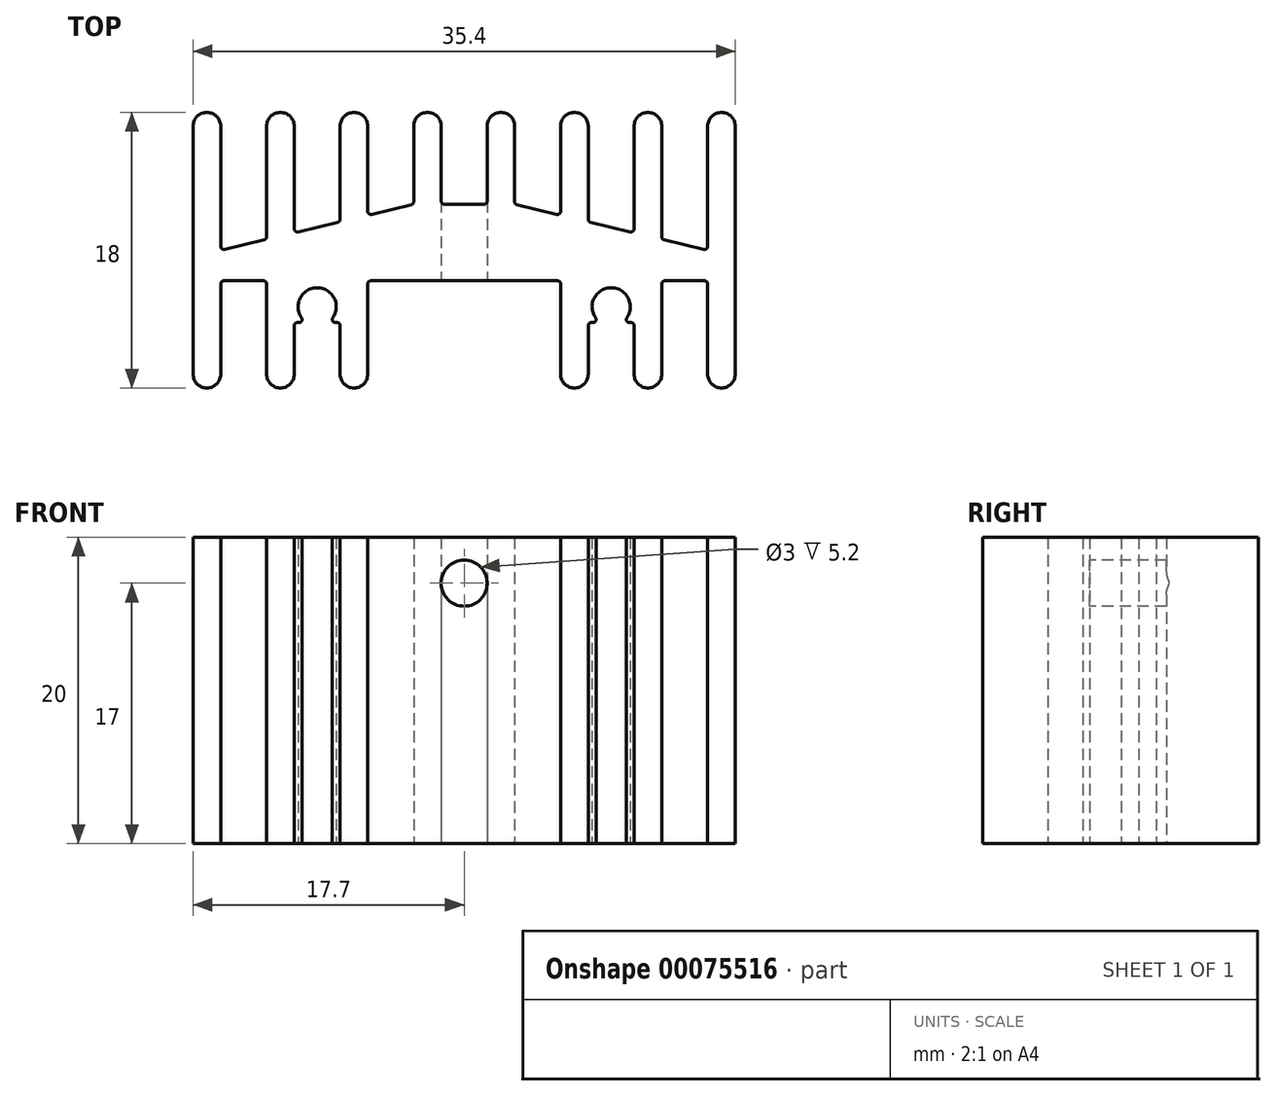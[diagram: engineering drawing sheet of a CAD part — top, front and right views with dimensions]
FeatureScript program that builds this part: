
annotation { "Feature Type Name" : "Feature", "Feature Type Description" : "" }
export const myFeature = defineFeature(function(context is Context, id is Id, definition is map)
    precondition{}
    {
        {
            var Q0;
            Q0=qCreatedBy(makeId("Top.planeOp"),FACE);
            var sketch = newSketch(context, id + "F0", { "sketchPlane" : qUnion([Q0])});
            skLineSegment(sketch, "E0", {"start": v(-17.7, 0) * mm, "end": v(-17.7, 10.1) * mm});
            skLineSegment(sketch, "E1", {"start": v(-17.7, 0) * mm, "end": v(-17.7, -6.1) * mm});
            skLineSegment(sketch, "E2.0", {"start": v(-15.9, -6.1) * mm, "end": v(-15.9, -2.93) * mm});
            skLineSegment(sketch, "E3.0", {"start": v(-12.9, -6.1) * mm, "end": v(-12.9, -2.93) * mm});
            skLineSegment(sketch, "E4.0", {"start": v(-11.1, -6.1) * mm, "end": v(-11.1, -2.93) * mm});
            skLineSegment(sketch, "E5.0", {"start": v(-8.1, -6.1) * mm, "end": v(-8.1, -2.93) * mm});
            skLineSegment(sketch, "E6.0", {"start": v(-6.3, -6.1) * mm, "end": v(-6.3, -0.2) * mm});
            skLineSegment(sketch, "E7.0", {"start": v(-3.3, 5.16) * mm, "end": v(-3.3, 10.1) * mm});
            skLineSegment(sketch, "E8.0", {"start": v(-1.5, 5.2) * mm, "end": v(-1.5, 10.1) * mm});
            skLineSegment(sketch, "E9", {"start": v(-16.8, -7) * mm, "end": v(-16.8, -7) * mm});
            skLineSegment(sketch, "E10", {"start": v(-16.8, 11) * mm, "end": v(-16.8, 11) * mm});
            skLineSegment(sketch, "E11.trimOffspring", {"start": v(-12, 11) * mm, "end": v(-12, 11) * mm});
            skLineSegment(sketch, "E12.trimOffspring", {"start": v(-7.2, 11) * mm, "end": v(-7.2, 11) * mm});
            skLineSegment(sketch, "E13.trimOffspring", {"start": v(-2.4, 11) * mm, "end": v(-2.4, 11) * mm});
            skLineSegment(sketch, "E14.trimOffspring", {"start": v(-7.2, -7) * mm, "end": v(-7.2, -7) * mm});
            skLineSegment(sketch, "E15.trimOffspring", {"start": v(-12, -7) * mm, "end": v(-12, -7) * mm});
            skPoint(sketch, "E16.orphan", {"position": v(0, -7) * mm});
            skLineSegment(sketch, "E17", {"start": v(-15.65, 2.06) * mm, "end": v(-13.05, 2.68) * mm});
            skLineSegment(sketch, "E18.trimOffspring", {"start": v(-11.1, 3.4) * mm, "end": v(-11.1, 10.1) * mm});
            skLineSegment(sketch, "E19.trimOffspring", {"start": v(-12.9, 2.87) * mm, "end": v(-12.9, 10.1) * mm});
            skLineSegment(sketch, "E20.trimOffspring", {"start": v(-8.1, 4.02) * mm, "end": v(-8.1, 10.1) * mm});
            skLineSegment(sketch, "E21.trimOffspring", {"start": v(-6.3, 4.54) * mm, "end": v(-6.3, 10.1) * mm});
            skLineSegment(sketch, "E22.trimOffspring", {"start": v(-6.05, 4.34) * mm, "end": v(-3.45, 4.96) * mm});
            skLineSegment(sketch, "E23.trimOffspring", {"start": v(-10.85, 3.2) * mm, "end": v(-8.25, 3.82) * mm});
            skLineSegment(sketch, "E24.trimOffspring", {"start": v(-15.9, 2.25) * mm, "end": v(-15.9, 10.1) * mm});
            skPoint(sketch, "E25.centerSnap0", {"position": v(-14.4, 0) * mm});
            skPoint(sketch, "E26.visualSharp", {"position": v(-1.5, 11) * mm});
            skArc(sketch, "E26.filletArc", {"start": v(-1.5, 10.1) * mm, "mid": v(-1.76, 10.74) * mm, "end": v(-2.4, 11) * mm});
            skPoint(sketch, "E27.visualSharp", {"position": v(-3.3, 11) * mm});
            skArc(sketch, "E27.filletArc", {"start": v(-2.4, 11) * mm, "mid": v(-3.04, 10.74) * mm, "end": v(-3.3, 10.1) * mm});
            skPoint(sketch, "E28.visualSharp", {"position": v(-6.3, 11) * mm});
            skArc(sketch, "E28.filletArc", {"start": v(-6.3, 10.1) * mm, "mid": v(-6.56, 10.74) * mm, "end": v(-7.2, 11) * mm});
            skPoint(sketch, "E29.visualSharp", {"position": v(-8.1, 11) * mm});
            skArc(sketch, "E29.filletArc", {"start": v(-7.2, 11) * mm, "mid": v(-7.84, 10.74) * mm, "end": v(-8.1, 10.1) * mm});
            skPoint(sketch, "E30.visualSharp", {"position": v(-11.1, 11) * mm});
            skArc(sketch, "E30.filletArc", {"start": v(-11.1, 10.1) * mm, "mid": v(-11.36, 10.74) * mm, "end": v(-12, 11) * mm});
            skPoint(sketch, "E31.visualSharp", {"position": v(-12.9, 11) * mm});
            skArc(sketch, "E31.filletArc", {"start": v(-12, 11) * mm, "mid": v(-12.64, 10.74) * mm, "end": v(-12.9, 10.1) * mm});
            skPoint(sketch, "E32.visualSharp", {"position": v(-15.9, 11) * mm});
            skArc(sketch, "E32.filletArc", {"start": v(-15.9, 10.1) * mm, "mid": v(-16.16, 10.74) * mm, "end": v(-16.8, 11) * mm});
            skPoint(sketch, "E33.visualSharp", {"position": v(-17.7, 11) * mm});
            skArc(sketch, "E33.filletArc", {"start": v(-16.8, 11) * mm, "mid": v(-17.44, 10.74) * mm, "end": v(-17.7, 10.1) * mm});
            skPoint(sketch, "E34.visualSharp", {"position": v(-17.7, -7) * mm});
            skArc(sketch, "E34.filletArc", {"start": v(-17.7, -6.1) * mm, "mid": v(-17.44, -6.74) * mm, "end": v(-16.8, -7) * mm});
            skPoint(sketch, "E35.visualSharp", {"position": v(-15.9, -7) * mm});
            skArc(sketch, "E35.filletArc", {"start": v(-16.8, -7) * mm, "mid": v(-16.16, -6.74) * mm, "end": v(-15.9, -6.1) * mm});
            skPoint(sketch, "E36.visualSharp", {"position": v(-12.9, -7) * mm});
            skArc(sketch, "E36.filletArc", {"start": v(-12.9, -6.1) * mm, "mid": v(-12.64, -6.74) * mm, "end": v(-12, -7) * mm});
            skPoint(sketch, "E37.visualSharp", {"position": v(-11.1, -7) * mm});
            skArc(sketch, "E37.filletArc", {"start": v(-12, -7) * mm, "mid": v(-11.36, -6.74) * mm, "end": v(-11.1, -6.1) * mm});
            skPoint(sketch, "E38.visualSharp", {"position": v(-8.1, -7) * mm});
            skArc(sketch, "E38.filletArc", {"start": v(-8.1, -6.1) * mm, "mid": v(-7.84, -6.74) * mm, "end": v(-7.2, -7) * mm});
            skPoint(sketch, "E39.visualSharp", {"position": v(-6.3, -7) * mm});
            skArc(sketch, "E39.filletArc", {"start": v(-7.2, -7) * mm, "mid": v(-6.56, -6.74) * mm, "end": v(-6.3, -6.1) * mm});
            skPoint(sketch, "E40.visualSharp", {"position": v(-12.9, 2.71) * mm});
            skArc(sketch, "E40.filletArc", {"start": v(-13.05, 2.68) * mm, "mid": v(-12.94, 2.75) * mm, "end": v(-12.9, 2.87) * mm});
            skPoint(sketch, "E41.visualSharp", {"position": v(-15.9, 2) * mm});
            skArc(sketch, "E41.filletArc", {"start": v(-15.9, 2.25) * mm, "mid": v(-15.82, 2.1) * mm, "end": v(-15.65, 2.06) * mm});
            skPoint(sketch, "E42.visualSharp", {"position": v(-11.1, 3.14) * mm});
            skArc(sketch, "E42.filletArc", {"start": v(-11.1, 3.4) * mm, "mid": v(-11.02, 3.24) * mm, "end": v(-10.85, 3.2) * mm});
            skPoint(sketch, "E43.visualSharp", {"position": v(-8.1, 3.86) * mm});
            skArc(sketch, "E43.filletArc", {"start": v(-8.25, 3.82) * mm, "mid": v(-8.14, 3.9) * mm, "end": v(-8.1, 4.02) * mm});
            skPoint(sketch, "E44.visualSharp", {"position": v(-6.3, 4.29) * mm});
            skArc(sketch, "E44.filletArc", {"start": v(-6.3, 4.54) * mm, "mid": v(-6.22, 4.38) * mm, "end": v(-6.05, 4.34) * mm});
            skPoint(sketch, "E45.visualSharp", {"position": v(-3.3, 5) * mm});
            skArc(sketch, "E45.filletArc", {"start": v(-3.45, 4.96) * mm, "mid": v(-3.34, 5.03) * mm, "end": v(-3.3, 5.16) * mm});
            skPoint(sketch, "E46.visualSharp", {"position": v(-1.5, 5) * mm});
            skArc(sketch, "E46.filletArc", {"start": v(-1.5, 5.2) * mm, "mid": v(-1.44, 5.06) * mm, "end": v(-1.3, 5) * mm});
            skPoint(sketch, "E47.visualSharp", {"position": v(-6.3, 0) * mm});
            skArc(sketch, "E47.filletArc", {"start": v(-6.1, 0) * mm, "mid": v(-6.24, -0.06) * mm, "end": v(-6.3, -0.2) * mm});
            skPoint(sketch, "E48.visualSharp", {"position": v(-8.1, 0) * mm});
            skPoint(sketch, "E49.visualSharp", {"position": v(-11.1, 0) * mm});
            skPoint(sketch, "E50.orphan", {"position": v(-15.9, 0) * mm});
            skPoint(sketch, "E51.orphan", {"position": v(-12.9, 0) * mm});
            skPoint(sketch, "E52.visualSharp", {"position": v(-15.9, -2.73) * mm});
            skPoint(sketch, "E53.visualSharp", {"position": v(-12.9, -2.73) * mm});
            skArc(sketch, "E54.MirrorCS", {"start": v(1.5, 5.2) * mm, "mid": v(1.44, 5.06) * mm, "end": v(1.3, 5) * mm});
            skArc(sketch, "E55.MirrorCS", {"start": v(13.05, 2.68) * mm, "mid": v(12.94, 2.75) * mm, "end": v(12.9, 2.87) * mm});
            skArc(sketch, "E56.MirrorCS", {"start": v(6.3, 4.54) * mm, "mid": v(6.22, 4.38) * mm, "end": v(6.05, 4.34) * mm});
            skArc(sketch, "E57.MirrorCS", {"start": v(8.25, 3.82) * mm, "mid": v(8.14, 3.9) * mm, "end": v(8.1, 4.02) * mm});
            skArc(sketch, "E58.MirrorCS", {"start": v(6.1, 0) * mm, "mid": v(6.24, -0.06) * mm, "end": v(6.3, -0.2) * mm});
            skArc(sketch, "E59.MirrorCS", {"start": v(1.5, 10.1) * mm, "mid": v(1.76, 10.74) * mm, "end": v(2.4, 11) * mm});
            skArc(sketch, "E60.MirrorCS", {"start": v(15.9, 2.25) * mm, "mid": v(15.82, 2.1) * mm, "end": v(15.65, 2.06) * mm});
            skArc(sketch, "E61.MirrorCS", {"start": v(2.4, 11) * mm, "mid": v(3.04, 10.74) * mm, "end": v(3.3, 10.1) * mm});
            skArc(sketch, "E62.MirrorCS", {"start": v(11.1, 3.4) * mm, "mid": v(11.02, 3.24) * mm, "end": v(10.85, 3.2) * mm});
            skArc(sketch, "E63.MirrorCS", {"start": v(12, -7) * mm, "mid": v(11.36, -6.74) * mm, "end": v(11.1, -6.1) * mm});
            skArc(sketch, "E64.MirrorCS", {"start": v(12.9, -6.1) * mm, "mid": v(12.64, -6.74) * mm, "end": v(12, -7) * mm});
            skArc(sketch, "E65.MirrorCS", {"start": v(8.1, -6.1) * mm, "mid": v(7.84, -6.74) * mm, "end": v(7.2, -7) * mm});
            skArc(sketch, "E66.MirrorCS", {"start": v(7.2, -7) * mm, "mid": v(6.56, -6.74) * mm, "end": v(6.3, -6.1) * mm});
            skArc(sketch, "E67.MirrorCS", {"start": v(6.3, 10.1) * mm, "mid": v(6.56, 10.74) * mm, "end": v(7.2, 11) * mm});
            skArc(sketch, "E68.MirrorCS", {"start": v(16.8, -7) * mm, "mid": v(16.16, -6.74) * mm, "end": v(15.9, -6.1) * mm});
            skArc(sketch, "E69.MirrorCS", {"start": v(7.2, 11) * mm, "mid": v(7.84, 10.74) * mm, "end": v(8.1, 10.1) * mm});
            skArc(sketch, "E70.MirrorCS", {"start": v(16.8, 11) * mm, "mid": v(17.44, 10.74) * mm, "end": v(17.7, 10.1) * mm});
            skArc(sketch, "E71.MirrorCS", {"start": v(12, 11) * mm, "mid": v(12.64, 10.74) * mm, "end": v(12.9, 10.1) * mm});
            skArc(sketch, "E72.MirrorCS", {"start": v(17.7, -6.1) * mm, "mid": v(17.44, -6.74) * mm, "end": v(16.8, -7) * mm});
            skPoint(sketch, "E73.MirrorP", {"position": v(12.9, -2.73) * mm});
            skPoint(sketch, "E74.MirrorP", {"position": v(15.11, -2.73) * mm});
            skPoint(sketch, "E75.MirrorP", {"position": v(13.69, -2.73) * mm});
            skArc(sketch, "E76.MirrorCS", {"start": v(15.9, 10.1) * mm, "mid": v(16.16, 10.74) * mm, "end": v(16.8, 11) * mm});
            skArc(sketch, "E77.MirrorCS", {"start": v(11.1, 10.1) * mm, "mid": v(11.36, 10.74) * mm, "end": v(12, 11) * mm});
            skPoint(sketch, "E78.MirrorP", {"position": v(12.9, 2.71) * mm});
            skPoint(sketch, "E79.MirrorP", {"position": v(15.9, -2.73) * mm});
            skLineSegment(sketch, "E80.MirrorCS", {"start": v(15.65, 2.06) * mm, "end": v(13.05, 2.68) * mm});
            skPoint(sketch, "E81.MirrorP", {"position": v(8.1, -7) * mm});
            skPoint(sketch, "E82.MirrorP", {"position": v(11.1, 11) * mm});
            skPoint(sketch, "E83.MirrorP", {"position": v(6.3, 4.29) * mm});
            skPoint(sketch, "E84.MirrorP", {"position": v(6.3, -7) * mm});
            skPoint(sketch, "E85.MirrorP", {"position": v(12.9, 11) * mm});
            skLineSegment(sketch, "E86.MirrorCS", {"start": v(16.8, -7) * mm, "end": v(16.8, -7) * mm});
            skPoint(sketch, "E87.MirrorP", {"position": v(3.3, 5) * mm});
            skLineSegment(sketch, "E88.MirrorCS", {"start": v(16.8, 11) * mm, "end": v(16.8, 11) * mm});
            skLineSegment(sketch, "E89.MirrorCS", {"start": v(12, 11) * mm, "end": v(12, 11) * mm});
            skPoint(sketch, "E90.MirrorP", {"position": v(1.5, 5) * mm});
            skPoint(sketch, "E91.MirrorP", {"position": v(15.9, 11) * mm});
            skLineSegment(sketch, "E92.MirrorCS", {"start": v(7.2, 11) * mm, "end": v(7.2, 11) * mm});
            skLineSegment(sketch, "E93.MirrorCS", {"start": v(2.4, 11) * mm, "end": v(2.4, 11) * mm});
            skPoint(sketch, "E94.MirrorP", {"position": v(6.3, 0) * mm});
            skPoint(sketch, "E95.MirrorP", {"position": v(17.7, 11) * mm});
            skPoint(sketch, "E96.MirrorP", {"position": v(14.4, 0) * mm});
            skLineSegment(sketch, "E97.MirrorCS", {"start": v(7.2, -7) * mm, "end": v(7.2, -7) * mm});
            skPoint(sketch, "E98.MirrorP", {"position": v(3.3, 11) * mm});
            skPoint(sketch, "E99.MirrorP", {"position": v(11.1, 0) * mm});
            skLineSegment(sketch, "E100.MirrorCS", {"start": v(15.9, 2.25) * mm, "end": v(15.9, 10.1) * mm});
            skPoint(sketch, "E101.MirrorP", {"position": v(15.9, 2) * mm});
            skPoint(sketch, "E102.MirrorP", {"position": v(12.9, -7) * mm});
            skPoint(sketch, "E103.MirrorP", {"position": v(17.7, -7) * mm});
            skLineSegment(sketch, "E104.MirrorCS", {"start": v(8.1, -6.1) * mm, "end": v(8.1, -2.93) * mm});
            skLineSegment(sketch, "E105.MirrorCS", {"start": v(12, -7) * mm, "end": v(12, -7) * mm});
            skPoint(sketch, "E106.MirrorP", {"position": v(8.1, 0) * mm});
            skLineSegment(sketch, "E107.MirrorCS", {"start": v(6.3, -6.1) * mm, "end": v(6.3, -0.2) * mm});
            skPoint(sketch, "E108.MirrorP", {"position": v(6.3, 11) * mm});
            skPoint(sketch, "E109.MirrorP", {"position": v(8.1, 3.86) * mm});
            skLineSegment(sketch, "E110.MirrorCS", {"start": v(3.3, 5.16) * mm, "end": v(3.3, 10.1) * mm});
            skLineSegment(sketch, "E111.MirrorCS", {"start": v(1.5, 5.2) * mm, "end": v(1.5, 10.1) * mm});
            skPoint(sketch, "E112.MirrorP", {"position": v(11.1, -7) * mm});
            skPoint(sketch, "E113.MirrorP", {"position": v(8.1, 11) * mm});
            skPoint(sketch, "E114.MirrorP", {"position": v(11.1, 3.14) * mm});
            skLineSegment(sketch, "E115.MirrorCS", {"start": v(8.1, 4.02) * mm, "end": v(8.1, 10.1) * mm});
            skPoint(sketch, "E116.MirrorP", {"position": v(15.9, -7) * mm});
            skLineSegment(sketch, "E117.MirrorCS", {"start": v(15.9, -6.1) * mm, "end": v(15.9, -2.93) * mm});
            skPoint(sketch, "E118.MirrorP", {"position": v(15.9, 0) * mm});
            skLineSegment(sketch, "E119.MirrorCS", {"start": v(17.7, 0) * mm, "end": v(17.7, -6.1) * mm});
            skLineSegment(sketch, "E120.MirrorCS", {"start": v(6.3, 4.54) * mm, "end": v(6.3, 10.1) * mm});
            skLineSegment(sketch, "E121.MirrorCS", {"start": v(11.1, -6.1) * mm, "end": v(11.1, -2.93) * mm});
            skLineSegment(sketch, "E122.MirrorCS", {"start": v(12.9, -6.1) * mm, "end": v(12.9, -2.93) * mm});
            skLineSegment(sketch, "E123.MirrorCS", {"start": v(11.1, 3.4) * mm, "end": v(11.1, 10.1) * mm});
            skLineSegment(sketch, "E124.MirrorCS", {"start": v(17.7, 0) * mm, "end": v(17.7, 10.1) * mm});
            skLineSegment(sketch, "E125.MirrorCS", {"start": v(10.85, 3.2) * mm, "end": v(8.25, 3.82) * mm});
            skPoint(sketch, "E126.MirrorP", {"position": v(1.5, 11) * mm});
            skLineSegment(sketch, "E127.MirrorCS", {"start": v(6.05, 4.34) * mm, "end": v(3.45, 4.96) * mm});
            skPoint(sketch, "E128.MirrorP", {"position": v(12.9, 0) * mm});
            skLineSegment(sketch, "E129.MirrorCS", {"start": v(12.9, 2.87) * mm, "end": v(12.9, 10.1) * mm});
            skLineSegment(sketch, "E130", {"start": v(-1.3, 5) * mm, "end": v(1.3, 5) * mm});
            skLineSegment(sketch, "E131", {"start": v(-6.1, 0) * mm, "end": v(6.1, 0) * mm});
            skArc(sketch, "E132.MirrorCS", {"start": v(3.45, 4.96) * mm, "mid": v(3.34, 5.03) * mm, "end": v(3.3, 5.16) * mm});
            skArc(sketch, "E133", {"start": v(-8.57, -2.41) * mm, "mid": v(-9.6, -0.45) * mm, "end": v(-10.63, -2.41) * mm});
            skPoint(sketch, "E133.centerSnap0", {"position": v(-9.6, 0) * mm});
            skLineSegment(sketch, "E134", {"start": v(-10.9, -2.73) * mm, "end": v(-10.8, -2.73) * mm});
            skLineSegment(sketch, "E135.trimOffspring", {"start": v(-8.4, -2.73) * mm, "end": v(-8.3, -2.73) * mm});
            skPoint(sketch, "E49.filletArc.end.orphan", {"position": v(-11.1, -0.2) * mm});
            skPoint(sketch, "E136.orphan", {"position": v(-10.9, 0) * mm});
            skPoint(sketch, "E48.filletArc.end.orphan", {"position": v(-8.3, 0) * mm});
            skPoint(sketch, "E137.orphan", {"position": v(-8.1, -0.2) * mm});
            skPoint(sketch, "E138.visualSharp", {"position": v(-8.89, -2.73) * mm});
            skArc(sketch, "E138.filletArc", {"start": v(-8.57, -2.41) * mm, "mid": v(-8.59, -2.62) * mm, "end": v(-8.4, -2.73) * mm});
            skPoint(sketch, "E139.visualSharp", {"position": v(-8.1, -2.73) * mm});
            skArc(sketch, "E139.filletArc", {"start": v(-8.1, -2.93) * mm, "mid": v(-8.16, -2.79) * mm, "end": v(-8.3, -2.73) * mm});
            skPoint(sketch, "E140.visualSharp", {"position": v(-10.31, -2.73) * mm});
            skArc(sketch, "E140.filletArc", {"start": v(-10.8, -2.73) * mm, "mid": v(-10.61, -2.62) * mm, "end": v(-10.63, -2.41) * mm});
            skPoint(sketch, "E141.visualSharp", {"position": v(-11.1, -2.73) * mm});
            skArc(sketch, "E141.filletArc", {"start": v(-10.9, -2.73) * mm, "mid": v(-11.04, -2.79) * mm, "end": v(-11.1, -2.93) * mm});
            skLineSegment(sketch, "E142", {"start": v(-15.9, -2.93) * mm, "end": v(-15.9, -0.2) * mm});
            skLineSegment(sketch, "E143", {"start": v(-15.7, 0) * mm, "end": v(-13.1, 0) * mm});
            skLineSegment(sketch, "E144", {"start": v(-12.9, -0.2) * mm, "end": v(-12.9, -2.93) * mm});
            skArc(sketch, "E145.filletArc", {"start": v(-12.9, -0.2) * mm, "mid": v(-12.96, -0.06) * mm, "end": v(-13.1, 0) * mm});
            skArc(sketch, "E146.filletArc", {"start": v(-15.7, 0) * mm, "mid": v(-15.84, -0.06) * mm, "end": v(-15.9, -0.2) * mm});
            skArc(sketch, "E147.MirrorCS", {"start": v(8.1, -2.93) * mm, "mid": v(8.16, -2.79) * mm, "end": v(8.3, -2.73) * mm});
            skLineSegment(sketch, "E148.MirrorCS", {"start": v(10.9, -2.73) * mm, "end": v(10.8, -2.73) * mm});
            skLineSegment(sketch, "E149.MirrorCS", {"start": v(8.4, -2.73) * mm, "end": v(8.3, -2.73) * mm});
            skArc(sketch, "E150.MirrorCS", {"start": v(8.57, -2.41) * mm, "mid": v(8.59, -2.62) * mm, "end": v(8.4, -2.73) * mm});
            skPoint(sketch, "E151.MirrorP", {"position": v(8.89, -2.73) * mm});
            skArc(sketch, "E152.MirrorCS", {"start": v(10.8, -2.73) * mm, "mid": v(10.61, -2.62) * mm, "end": v(10.63, -2.41) * mm});
            skPoint(sketch, "E153.MirrorP", {"position": v(10.31, -2.73) * mm});
            skArc(sketch, "E154.MirrorCS", {"start": v(10.9, -2.73) * mm, "mid": v(11.04, -2.79) * mm, "end": v(11.1, -2.93) * mm});
            skArc(sketch, "E155.MirrorCS", {"start": v(8.57, -2.41) * mm, "mid": v(9.6, -0.45) * mm, "end": v(10.63, -2.41) * mm});
            skPoint(sketch, "E156.MirrorCS.start.orphan", {"position": v(8.1, -0.2) * mm});
            skPoint(sketch, "E157.MirrorCS.start.orphan", {"position": v(8.3, 0) * mm});
            skPoint(sketch, "E158.MirrorCS.end.orphan", {"position": v(11.1, -0.2) * mm});
            skPoint(sketch, "E158.MirrorCS.start.orphan", {"position": v(10.9, 0) * mm});
            skLineSegment(sketch, "E159", {"start": v(12.9, -2.93) * mm, "end": v(12.9, -0.2) * mm});
            skLineSegment(sketch, "E160", {"start": v(13.1, 0) * mm, "end": v(15.7, 0) * mm});
            skLineSegment(sketch, "E161", {"start": v(15.9, -0.2) * mm, "end": v(15.9, -2.93) * mm});
            skArc(sketch, "E162.filletArc", {"start": v(13.1, 0) * mm, "mid": v(12.96, -0.06) * mm, "end": v(12.9, -0.2) * mm});
            skArc(sketch, "E163.filletArc", {"start": v(15.9, -0.2) * mm, "mid": v(15.84, -0.06) * mm, "end": v(15.7, 0) * mm});
            skSolve(sketch);
        }
        {
            var Q0;
            Q0 = qSketchRegion(id + "F0", true);
            extrude(context, id + "F1", {"entities" : qUnion([Q0]), "depth" : 20 * mm});
        }
        {
            var Q0;
            Q0=makeQuery(id+"F1.opExtrude","SWEPT_FACE",FACE,{"disambiguationData":[OSD([sQuery(id+"F0.wireOp",EDGE,"E131")])]});
            var sketch = newSketch(context, id + "F2", { "sketchPlane" : qUnion([Q0])});
            skCircle(sketch, "E164", {"center": v(0, 17) * mm, "radius": 1.5 * mm});
            skSolve(sketch);
        }
        {
            var Q0;
            Q0 = qSketchRegion(id + "F2", true);
            extrude(context, id + "F3", {"entities" : qUnion([Q0]), "operationType" : NewBodyOperationType.REMOVE, "endBound" : BoundingType.UP_TO_NEXT, "oppositeDirection" : true, "depth" : 25 * mm});
        }
    });
